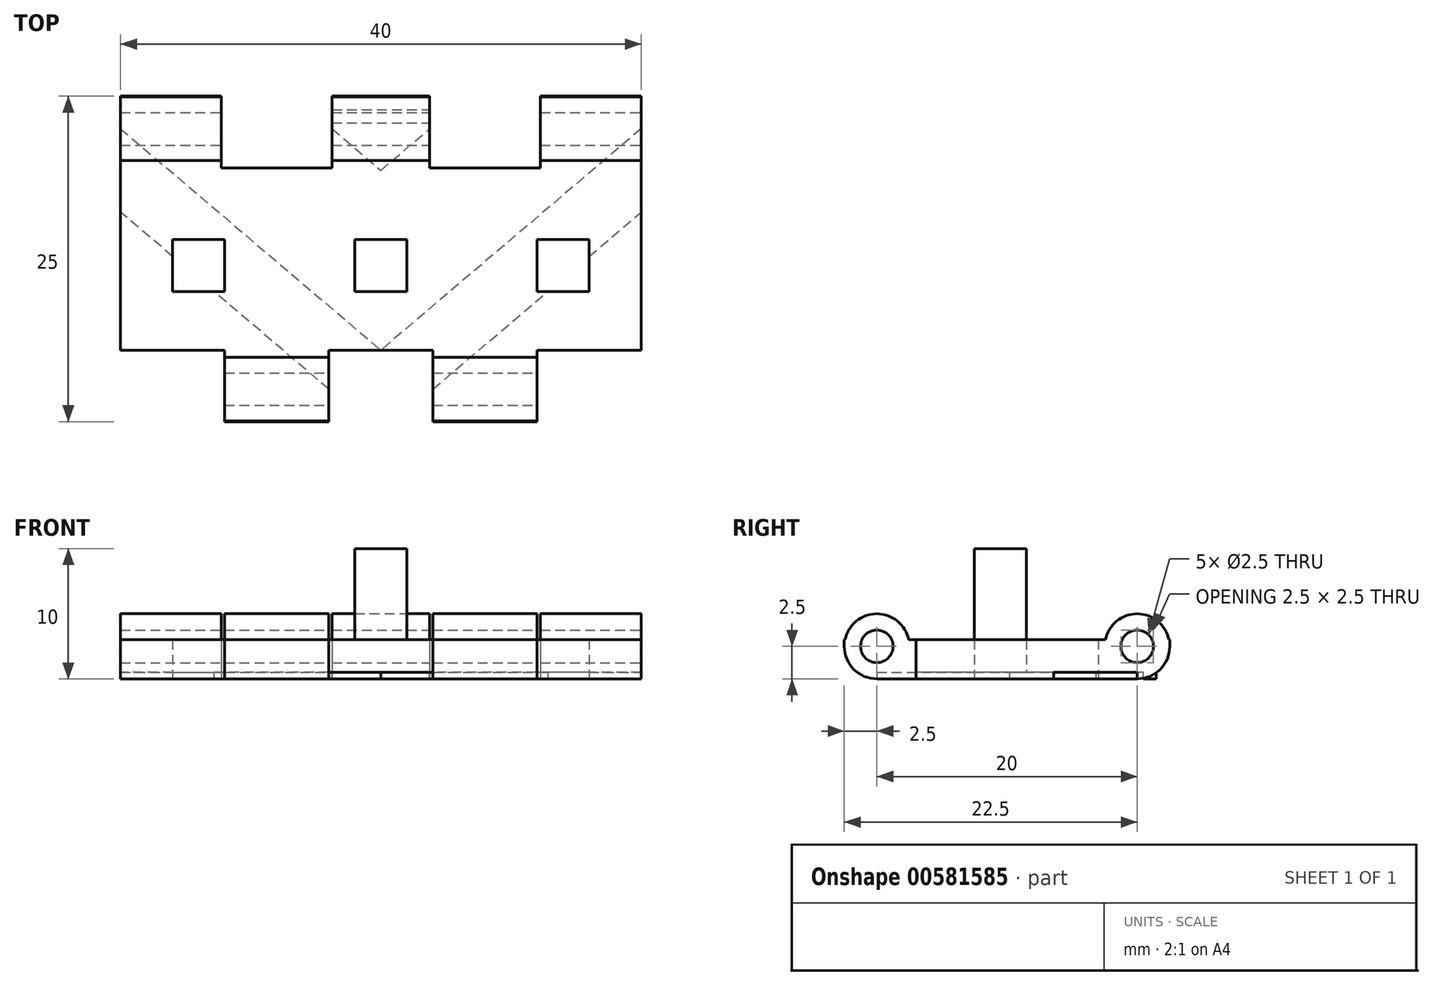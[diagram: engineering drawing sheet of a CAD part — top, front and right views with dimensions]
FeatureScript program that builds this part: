
annotation { "Feature Type Name" : "Feature", "Feature Type Description" : "" }
export const myFeature = defineFeature(function(context is Context, id is Id, definition is map)
    precondition{}
    {
        {
            var Q0;
            Q0=qCreatedBy(makeId("Top.planeOp"),FACE);
            var sketch = newSketch(context, id + "F0", { "sketchPlane" : qUnion([Q0])});
            skPoint(sketch, "E0.middle", {"position": v(0, 0) * mm});
            skLineSegment(sketch, "E1.top", {"start": v(-20, 15) * mm, "end": v(-12.25, 15) * mm});
            skLineSegment(sketch, "E1.left", {"start": v(-20, 10) * mm, "end": v(-20, 15) * mm});
            skLineSegment(sketch, "E1.right", {"start": v(-12.25, 10) * mm, "end": v(-12.25, 15) * mm});
            skLineSegment(sketch, "E2.top", {"start": v(20, 15) * mm, "end": v(12.25, 15) * mm});
            skLineSegment(sketch, "E2.left", {"start": v(20, 10) * mm, "end": v(20, 15) * mm});
            skLineSegment(sketch, "E2.right", {"start": v(12.25, 11) * mm, "end": v(12.25, 15) * mm});
            skLineSegment(sketch, "E3.top", {"start": v(-3.75, 15) * mm, "end": v(3.75, 15) * mm});
            skLineSegment(sketch, "E3.left", {"start": v(-3.75, 10) * mm, "end": v(-3.75, 15) * mm});
            skLineSegment(sketch, "E3.right", {"start": v(3.75, 11) * mm, "end": v(3.75, 15) * mm});
            skLineSegment(sketch, "E4.top", {"start": v(-20, -6) * mm, "end": v(-12, -6) * mm});
            skLineSegment(sketch, "E4.right", {"start": v(-12, -10) * mm, "end": v(-12, -6) * mm});
            skLineSegment(sketch, "E5.top", {"start": v(20, -6) * mm, "end": v(12, -6) * mm});
            skLineSegment(sketch, "E5.right", {"start": v(12, -10) * mm, "end": v(12, -6) * mm});
            skLineSegment(sketch, "E6.top", {"start": v(4, -6) * mm, "end": v(-4, -6) * mm});
            skLineSegment(sketch, "E6.left", {"start": v(4, -10) * mm, "end": v(4, -6) * mm});
            skLineSegment(sketch, "E6.right", {"start": v(-4, -10) * mm, "end": v(-4, -6) * mm});
            skLineSegment(sketch, "E7", {"start": v(-20, 10) * mm, "end": v(-20, -6) * mm});
            skLineSegment(sketch, "E8", {"start": v(-12, -10) * mm, "end": v(-4, -10) * mm});
            skLineSegment(sketch, "E9", {"start": v(4, -10) * mm, "end": v(12, -10) * mm});
            skLineSegment(sketch, "E10", {"start": v(20, -6) * mm, "end": v(20, 10) * mm});
            skLineSegment(sketch, "E11", {"start": v(-12.25, 10) * mm, "end": v(-3.75, 10) * mm});
            skLineSegment(sketch, "E12", {"start": v(3.75, 11) * mm, "end": v(12.25, 11) * mm});
            skSolve(sketch);
        }
        {
            var Q0;
            Q0=makeQuery(id+"F0.imprint","IMPRINT",FACE,{"disambiguationData":[TD([[makeQuery(id+"F0.imprint","IMPRINT",EDGE,{"derivedFrom":sQuery(id+"F0.wireOp",EDGE,"E1.top")}),-1.0]])]});
            var sketch = newSketch(context, id + "F1", { "sketchPlane" : qUnion([Q0])});
            skLineSegment(sketch, "E13.bottom", {"start": v(-16, 0) * mm, "end": v(-12, 0) * mm});
            skLineSegment(sketch, "E13.top", {"start": v(-16, 4) * mm, "end": v(-12, 4) * mm});
            skLineSegment(sketch, "E13.left", {"start": v(-16, 0) * mm, "end": v(-16, 4) * mm});
            skLineSegment(sketch, "E13.right", {"start": v(-12, 0) * mm, "end": v(-12, 4) * mm});
            skLineSegment(sketch, "E14.bottom", {"start": v(16, 0) * mm, "end": v(12, 0) * mm});
            skLineSegment(sketch, "E14.top", {"start": v(16, 4) * mm, "end": v(12, 4) * mm});
            skLineSegment(sketch, "E14.left", {"start": v(16, 0) * mm, "end": v(16, 4) * mm});
            skLineSegment(sketch, "E14.right", {"start": v(12, 0) * mm, "end": v(12, 4) * mm});
            skSolve(sketch);
        }
        {
            var Q0;
            Q0=makeQuery(id+"F0.imprint","IMPRINT",FACE,{"disambiguationData":[TD([[makeQuery(id+"F0.imprint","IMPRINT",EDGE,{"derivedFrom":sQuery(id+"F0.wireOp",EDGE,"E1.top")}),-1.0]])]});
            extrude(context, id + "F2", {"entities" : qUnion([Q0]), "depth" : 3 * mm, "offsetDistance" : 25 * mm});
        }
        {
            var Q0;
            Q0 = qSketchRegion(id + "F1", true);
            extrude(context, id + "F3", {"entities" : qUnion([Q0]), "operationType" : NewBodyOperationType.REMOVE, "depth" : 3 * mm, "offsetDistance" : 25 * mm});
        }
        {
            var Q0;
            Q0=qCreatedBy(makeId("Top.planeOp"),FACE);
            var sketch = newSketch(context, id + "F4", { "sketchPlane" : qUnion([Q0])});
            skLineSegment(sketch, "E15.bottom", {"start": v(2, 0) * mm, "end": v(-2, 0) * mm});
            skLineSegment(sketch, "E15.top", {"start": v(2, 4) * mm, "end": v(-2, 4) * mm});
            skLineSegment(sketch, "E15.left", {"start": v(2, 0) * mm, "end": v(2, 4) * mm});
            skLineSegment(sketch, "E15.right", {"start": v(-2, 0) * mm, "end": v(-2, 4) * mm});
            skSolve(sketch);
        }
        {
            var Q0;
            Q0 = qSketchRegion(id + "F4", true);
            extrude(context, id + "F5", {"entities" : qUnion([Q0]), "operationType" : NewBodyOperationType.ADD, "depth" : 10 * mm, "offsetDistance" : 25 * mm});
        }
        {
            var Q0;
            Q0=makeQuery(id+"F2.opExtrude","SWEPT_FACE",FACE,{"disambiguationData":[OSD([sQuery(id+"F0.wireOp",EDGE,"E2.left"),sQuery(id+"F0.wireOp",EDGE,"E10")])]});
            var sketch = newSketch(context, id + "F6", { "sketchPlane" : qUnion([Q0])});
            skCircle(sketch, "E16", {"center": v(12.5, 2.5) * mm, "radius": 2.5 * mm});
            skCircle(sketch, "E17", {"center": v(12.5, 2.5) * mm, "radius": 1.25 * mm});
            skSolve(sketch);
        }
        {
            var Q0;
            {var subQ0=sQuery(id+"F6.wireOp",EDGE,"E16");var subQ1=makeQuery(id+"F2.opExtrude","CAP_EDGE",EDGE,{"disambiguationData":[OSD([sQuery(id+"F0.wireOp",EDGE,"E2.left"),sQuery(id+"F0.wireOp",EDGE,"E10")])],"isStart":false});var subQ2=makeQuery(id+"F6.imprint","INTERSECT",VERTEX,{"disambiguationData":[OD(0.0)],"derivedFrom":[subQ1,subQ0]});Q0=makeQuery(id+"F6.imprint","IMPRINT",FACE,{"disambiguationData":[TD([[makeQuery(id+"F6.imprint","IMPRINT",EDGE,{"disambiguationData":[TD([[subQ2,-1.0]])],"derivedFrom":subQ0}),1.0]])]});}
            extrude(context, id + "F7", {"entities" : qUnion([Q0]), "operationType" : NewBodyOperationType.ADD, "oppositeDirection" : true, "depth" : 40 * mm, "offsetDistance" : 25 * mm});
        }
        {
            var Q0;
            {var subQ0=sQuery(id+"F6.wireOp",EDGE,"E17");var subQ1=makeQuery(id+"F2.opExtrude","CAP_EDGE",EDGE,{"disambiguationData":[OSD([sQuery(id+"F0.wireOp",EDGE,"E2.left"),sQuery(id+"F0.wireOp",EDGE,"E10")])],"isStart":false});var subQ2=makeQuery(id+"F6.imprint","INTERSECT",VERTEX,{"disambiguationData":[OD(0.0)],"derivedFrom":[subQ1,subQ0]});Q0=makeQuery(id+"F6.imprint","IMPRINT",FACE,{"disambiguationData":[TD([[makeQuery(id+"F6.imprint","IMPRINT",EDGE,{"disambiguationData":[TD([[subQ2,1.0]])],"derivedFrom":subQ0}),1.0]])]});}
            extrude(context, id + "F8", {"entities" : qUnion([Q0]), "operationType" : NewBodyOperationType.REMOVE, "oppositeDirection" : true, "depth" : 40 * mm, "offsetDistance" : 25 * mm});
        }
        {
            var Q0;
            {var subQ0=sQuery(id+"F6.wireOp",EDGE,"E16");var subQ1=sQuery(id+"F0.wireOp",EDGE,"E2.left");var subQ2=makeQuery(id+"F2.opExtrude","SWEPT_EDGE",EDGE,{"disambiguationData":[OSD([sQuery(id+"F0.wireOp",EDGE,"E2.top"),subQ1])]});var subQ3=makeQuery(id+"F6.imprint","INTERSECT",VERTEX,{"derivedFrom":[subQ2,subQ0]});Q0=makeQuery(id+"F6.imprint","IMPRINT",FACE,{"disambiguationData":[TD([[makeQuery(id+"F6.imprint","IMPRINT",EDGE,{"disambiguationData":[TD([[subQ3,1.0]])],"derivedFrom":subQ0}),-1.0]])]});}
            extrude(context, id + "F9", {"entities" : qUnion([Q0]), "operationType" : NewBodyOperationType.REMOVE, "oppositeDirection" : true, "depth" : 40 * mm, "offsetDistance" : 25 * mm});
        }
        {
            var Q0;
            Q0=makeQuery(id+"F2.opExtrude","CAP_FACE",FACE,{"disambiguationData":[OSD([sQuery(id+"F0.wireOp",EDGE,"E1.top"),sQuery(id+"F0.wireOp",EDGE,"E1.left"),sQuery(id+"F0.wireOp",EDGE,"E1.right"),sQuery(id+"F0.wireOp",EDGE,"E2.top"),sQuery(id+"F0.wireOp",EDGE,"E2.left"),sQuery(id+"F0.wireOp",EDGE,"E2.right"),sQuery(id+"F0.wireOp",EDGE,"E3.top"),sQuery(id+"F0.wireOp",EDGE,"E3.left"),sQuery(id+"F0.wireOp",EDGE,"E3.right"),sQuery(id+"F0.wireOp",EDGE,"E4.top"),sQuery(id+"F0.wireOp",EDGE,"E4.right"),sQuery(id+"F0.wireOp",EDGE,"E5.top"),sQuery(id+"F0.wireOp",EDGE,"E5.right"),sQuery(id+"F0.wireOp",EDGE,"E6.top"),sQuery(id+"F0.wireOp",EDGE,"E6.left"),sQuery(id+"F0.wireOp",EDGE,"E6.right"),sQuery(id+"F0.wireOp",EDGE,"E7"),sQuery(id+"F0.wireOp",EDGE,"E8"),sQuery(id+"F0.wireOp",EDGE,"E9"),sQuery(id+"F0.wireOp",EDGE,"E10"),sQuery(id+"F0.wireOp",EDGE,"E11"),sQuery(id+"F0.wireOp",EDGE,"E12")])],"isStart":true});
            var sketch = newSketch(context, id + "F10", { "sketchPlane" : qUnion([Q0])});
            skLineSegment(sketch, "E18.bottom", {"start": v(12.25, -11) * mm, "end": v(3.75, -11) * mm});
            skLineSegment(sketch, "E18.top", {"start": v(12.25, -16.51) * mm, "end": v(3.75, -16.51) * mm});
            skLineSegment(sketch, "E18.left", {"start": v(12.25, -11) * mm, "end": v(12.25, -16.51) * mm});
            skLineSegment(sketch, "E18.right", {"start": v(3.75, -11) * mm, "end": v(3.75, -16.51) * mm});
            skLineSegment(sketch, "E19.bottom", {"start": v(-3.75, -10) * mm, "end": v(-12.25, -10) * mm});
            skLineSegment(sketch, "E19.top", {"start": v(-3.75, -16.05) * mm, "end": v(-12.25, -16.05) * mm});
            skLineSegment(sketch, "E19.left", {"start": v(-3.75, -10) * mm, "end": v(-3.75, -16.05) * mm});
            skLineSegment(sketch, "E19.right", {"start": v(-12.25, -10) * mm, "end": v(-12.25, -16.05) * mm});
            skSolve(sketch);
        }
        {
            var Q0;
            Q0 = qSketchRegion(id + "F10", true);
            extrude(context, id + "F11", {"entities" : qUnion([Q0]), "operationType" : NewBodyOperationType.REMOVE, "oppositeDirection" : true, "depth" : 5 * mm, "offsetDistance" : 25 * mm});
        }
        {
            var Q0;
            Q0=makeQuery(id+"F2.opExtrude","SWEPT_FACE",FACE,{"disambiguationData":[OSD([sQuery(id+"F0.wireOp",EDGE,"E5.right")])]});
            var sketch = newSketch(context, id + "F12", { "sketchPlane" : qUnion([Q0])});
            skCircle(sketch, "E20", {"center": v(-7.5, 2.5) * mm, "radius": 2.5 * mm});
            skCircle(sketch, "E21", {"center": v(-7.5, 2.5) * mm, "radius": 1.25 * mm});
            skSolve(sketch);
        }
        {
            var Q0;
            {var subQ0=sQuery(id+"F0.wireOp",EDGE,"E5.right");var subQ1=makeQuery(id+"F2.opExtrude","CAP_EDGE",EDGE,{"disambiguationData":[OSD([subQ0])],"isStart":false});var subQ6=sQuery(id+"F12.wireOp",EDGE,"E21");var subQ7=makeQuery(id+"F12.imprint","INTERSECT",VERTEX,{"disambiguationData":[OD(0.0)],"derivedFrom":[subQ1,subQ6]});Q0=makeQuery(id+"F12.imprint","IMPRINT",FACE,{"disambiguationData":[TD([[makeQuery(id+"F12.imprint","IMPRINT",EDGE,{"disambiguationData":[TD([[subQ7,-1.0]])],"derivedFrom":subQ6}),-1.0]])]});}
            extrude(context, id + "F13", {"entities" : qUnion([Q0]), "operationType" : NewBodyOperationType.ADD, "oppositeDirection" : true, "depth" : 24 * mm, "offsetDistance" : 25 * mm});
        }
        {
            var Q0;
            Q0=makeQuery(id+"F2.opExtrude","CAP_FACE",FACE,{"disambiguationData":[OSD([sQuery(id+"F0.wireOp",EDGE,"E1.top"),sQuery(id+"F0.wireOp",EDGE,"E1.left"),sQuery(id+"F0.wireOp",EDGE,"E1.right"),sQuery(id+"F0.wireOp",EDGE,"E2.top"),sQuery(id+"F0.wireOp",EDGE,"E2.left"),sQuery(id+"F0.wireOp",EDGE,"E2.right"),sQuery(id+"F0.wireOp",EDGE,"E3.top"),sQuery(id+"F0.wireOp",EDGE,"E3.left"),sQuery(id+"F0.wireOp",EDGE,"E3.right"),sQuery(id+"F0.wireOp",EDGE,"E4.top"),sQuery(id+"F0.wireOp",EDGE,"E4.right"),sQuery(id+"F0.wireOp",EDGE,"E5.top"),sQuery(id+"F0.wireOp",EDGE,"E5.right"),sQuery(id+"F0.wireOp",EDGE,"E6.top"),sQuery(id+"F0.wireOp",EDGE,"E6.left"),sQuery(id+"F0.wireOp",EDGE,"E6.right"),sQuery(id+"F0.wireOp",EDGE,"E7"),sQuery(id+"F0.wireOp",EDGE,"E8"),sQuery(id+"F0.wireOp",EDGE,"E9"),sQuery(id+"F0.wireOp",EDGE,"E10"),sQuery(id+"F0.wireOp",EDGE,"E11"),sQuery(id+"F0.wireOp",EDGE,"E12")])],"isStart":true});
            var sketch = newSketch(context, id + "F14", { "sketchPlane" : qUnion([Q0])});
            skPoint(sketch, "E22.oppositeSnap0", {"position": v(4, 8) * mm});
            skLineSegment(sketch, "E22.bottom", {"start": v(-4, 6) * mm, "end": v(4, 6) * mm});
            skLineSegment(sketch, "E22.top", {"start": v(-4, 10.57) * mm, "end": v(4, 10.57) * mm});
            skLineSegment(sketch, "E22.left", {"start": v(-4, 6) * mm, "end": v(-4, 10.57) * mm});
            skLineSegment(sketch, "E22.right", {"start": v(4, 6) * mm, "end": v(4, 10.57) * mm});
            skSolve(sketch);
        }
        {
            var Q0;
            {var subQ3=sQuery(id+"F14.wireOp",EDGE,"E22.bottom");Q0=makeQuery(id+"F14.imprint","IMPRINT",FACE,{"disambiguationData":[TD([[makeQuery(id+"F14.imprint","IMPRINT",EDGE,{"derivedFrom":subQ3}),-1.0]])]});}
            extrude(context, id + "F15", {"entities" : qUnion([Q0]), "operationType" : NewBodyOperationType.REMOVE, "oppositeDirection" : true, "depth" : 5 * mm, "offsetDistance" : 25 * mm});
        }
        {
            var Q0;
            {var subQ0=sQuery(id+"F12.wireOp",EDGE,"E21");var subQ1=makeQuery(id+"F2.opExtrude","CAP_EDGE",EDGE,{"disambiguationData":[OSD([sQuery(id+"F0.wireOp",EDGE,"E5.right")])],"isStart":false});var subQ2=makeQuery(id+"F12.imprint","INTERSECT",VERTEX,{"disambiguationData":[OD(0.0)],"derivedFrom":[subQ1,subQ0]});Q0=makeQuery(id+"F12.imprint","IMPRINT",FACE,{"disambiguationData":[TD([[makeQuery(id+"F12.imprint","IMPRINT",EDGE,{"disambiguationData":[TD([[subQ2,1.0]])],"derivedFrom":subQ0}),1.0]])]});}
            extrude(context, id + "F16", {"entities" : qUnion([Q0]), "operationType" : NewBodyOperationType.REMOVE, "oppositeDirection" : true, "depth" : 24 * mm, "offsetDistance" : 25 * mm});
        }
        {
            var Q0;
            {var subQ0=sQuery(id+"F12.wireOp",EDGE,"E20");var subQ1=sQuery(id+"F0.wireOp",EDGE,"E5.right");var subQ4=makeQuery(id+"F2.opExtrude","CAP_EDGE",EDGE,{"disambiguationData":[OSD([subQ1])],"isStart":true});var subQ5=makeQuery(id+"F12.imprint","INTERSECT",VERTEX,{"derivedFrom":[subQ4,subQ0]});Q0=makeQuery(id+"F12.imprint","IMPRINT",FACE,{"disambiguationData":[TD([[makeQuery(id+"F12.imprint","IMPRINT",EDGE,{"disambiguationData":[TD([[subQ5,1.0]])],"derivedFrom":subQ0}),-1.0]])]});}
            extrude(context, id + "F17", {"entities" : qUnion([Q0]), "operationType" : NewBodyOperationType.REMOVE, "oppositeDirection" : true, "depth" : 24 * mm, "offsetDistance" : 25 * mm});
        }
        {
            var Q0;
            Q0=makeQuery(id+"F11.boolean.opBoolean","MERGE",FACE,{"derivedFrom":[makeQuery(id+"F2.opExtrude","SWEPT_FACE",FACE,{"disambiguationData":[OSD([sQuery(id+"F0.wireOp",EDGE,"E12")])]}),makeQuery(id+"F11.opExtrude","SWEPT_FACE",FACE,{"disambiguationData":[OSD([sQuery(id+"F10.wireOp",EDGE,"E18.bottom")])]})]});
            var Q1;
            Q1=makeQuery(id+"F11.boolean.opBoolean","MERGE",FACE,{"derivedFrom":[makeQuery(id+"F2.opExtrude","SWEPT_FACE",FACE,{"disambiguationData":[OSD([sQuery(id+"F0.wireOp",EDGE,"E11")])]}),makeQuery(id+"F11.opExtrude","SWEPT_FACE",FACE,{"disambiguationData":[OSD([sQuery(id+"F10.wireOp",EDGE,"E19.bottom")])]})]});
            extrude(context, id + "F18", {"entities" : qUnion([Q0, Q1]), "operationType" : NewBodyOperationType.REMOVE, "oppositeDirection" : true, "depth" : 1.5 * mm, "offsetDistance" : 25 * mm});
        }
        {
            var Q0;
            Q0=makeQuery(id+"F15.boolean.opBoolean","MERGE",FACE,{"derivedFrom":[makeQuery(id+"F2.opExtrude","SWEPT_FACE",FACE,{"disambiguationData":[OSD([sQuery(id+"F0.wireOp",EDGE,"E6.top")])]}),makeQuery(id+"F15.opExtrude","SWEPT_FACE",FACE,{"disambiguationData":[OSD([sQuery(id+"F14.wireOp",EDGE,"E22.bottom")])]})]});
            var Q1;
            Q1=makeQuery(id+"F2.opExtrude","SWEPT_FACE",FACE,{"disambiguationData":[OSD([sQuery(id+"F0.wireOp",EDGE,"E4.top")])]});
            var Q2;
            Q2=makeQuery(id+"F2.opExtrude","SWEPT_FACE",FACE,{"disambiguationData":[OSD([sQuery(id+"F0.wireOp",EDGE,"E5.top")])]});
            extrude(context, id + "F19", {"entities" : qUnion([Q0, Q1, Q2]), "operationType" : NewBodyOperationType.REMOVE, "oppositeDirection" : true, "depth" : 1.5 * mm, "offsetDistance" : 25 * mm});
        }
        {
            var Q0;
            Q0=makeQuery(id+"F2.opExtrude","CAP_FACE",FACE,{"disambiguationData":[OSD([sQuery(id+"F0.wireOp",EDGE,"E1.top"),sQuery(id+"F0.wireOp",EDGE,"E1.left"),sQuery(id+"F0.wireOp",EDGE,"E1.right"),sQuery(id+"F0.wireOp",EDGE,"E2.top"),sQuery(id+"F0.wireOp",EDGE,"E2.left"),sQuery(id+"F0.wireOp",EDGE,"E2.right"),sQuery(id+"F0.wireOp",EDGE,"E3.top"),sQuery(id+"F0.wireOp",EDGE,"E3.left"),sQuery(id+"F0.wireOp",EDGE,"E3.right"),sQuery(id+"F0.wireOp",EDGE,"E4.top"),sQuery(id+"F0.wireOp",EDGE,"E4.right"),sQuery(id+"F0.wireOp",EDGE,"E5.top"),sQuery(id+"F0.wireOp",EDGE,"E5.right"),sQuery(id+"F0.wireOp",EDGE,"E6.top"),sQuery(id+"F0.wireOp",EDGE,"E6.left"),sQuery(id+"F0.wireOp",EDGE,"E6.right"),sQuery(id+"F0.wireOp",EDGE,"E7"),sQuery(id+"F0.wireOp",EDGE,"E8"),sQuery(id+"F0.wireOp",EDGE,"E9"),sQuery(id+"F0.wireOp",EDGE,"E10"),sQuery(id+"F0.wireOp",EDGE,"E11"),sQuery(id+"F0.wireOp",EDGE,"E12")])],"isStart":true});
            var sketch = newSketch(context, id + "F20", { "sketchPlane" : qUnion([Q0])});
            skLineSegment(sketch, "E23", {"start": v(-20, -12.5) * mm, "end": v(0, 4.5) * mm});
            skLineSegment(sketch, "E24", {"start": v(0, 4.5) * mm, "end": v(-4, 7.5) * mm});
            skLineSegment(sketch, "E25", {"start": v(-4, 7.5) * mm, "end": v(-20, -6.1) * mm});
            skLineSegment(sketch, "E26", {"start": v(-20, -6.1) * mm, "end": v(-20, -12.5) * mm});
            skLineSegment(sketch, "E27", {"start": v(20, -12.5) * mm, "end": v(0, 4.5) * mm});
            skLineSegment(sketch, "E28", {"start": v(0, 4.5) * mm, "end": v(4, 7.5) * mm});
            skLineSegment(sketch, "E29", {"start": v(4, 7.5) * mm, "end": v(20, -6.1) * mm});
            skLineSegment(sketch, "E30", {"start": v(20, -6.1) * mm, "end": v(20, -12.5) * mm});
            skSolve(sketch);
        }
        {
            var Q0;
            {var subQ18=sQuery(id+"F20.wireOp",EDGE,"E23");Q0=makeQuery(id+"F20.imprint","IMPRINT",FACE,{"disambiguationData":[TD([[makeQuery(id+"F20.imprint","IMPRINT",EDGE,{"derivedFrom":subQ18}),1.0]])]});}
            var Q1;
            {var subQ11=sQuery(id+"F20.wireOp",EDGE,"E27");Q1=makeQuery(id+"F20.imprint","IMPRINT",FACE,{"disambiguationData":[TD([[makeQuery(id+"F20.imprint","IMPRINT",EDGE,{"derivedFrom":subQ11}),-1.0]])]});}
            extrude(context, id + "F21", {"entities" : qUnion([Q0, Q1]), "operationType" : NewBodyOperationType.REMOVE, "oppositeDirection" : true, "depth" : .5 * mm, "offsetDistance" : 25 * mm});
        }
        {
            var Q0;
            {var subQ0=sQuery(id+"F0.wireOp",EDGE,"E1.right");var subQ1=makeQuery(id+"F2.opExtrude","SWEPT_FACE",FACE,{"disambiguationData":[OSD([subQ0])]});var subQ2=sQuery(id+"F0.wireOp",EDGE,"E7");var subQ3=sQuery(id+"F0.wireOp",EDGE,"E1.left");var subQ5=sQuery(id+"F0.wireOp",EDGE,"E12");var subQ6=sQuery(id+"F0.wireOp",EDGE,"E11");var subQ7=sQuery(id+"F0.wireOp",EDGE,"E10");var subQ8=sQuery(id+"F0.wireOp",EDGE,"E3.right");var subQ9=sQuery(id+"F0.wireOp",EDGE,"E3.left");var subQ10=sQuery(id+"F0.wireOp",EDGE,"E3.top");var subQ11=sQuery(id+"F0.wireOp",EDGE,"E2.right");var subQ12=sQuery(id+"F0.wireOp",EDGE,"E2.left");var subQ13=sQuery(id+"F0.wireOp",EDGE,"E2.top");var subQ14=sQuery(id+"F0.wireOp",EDGE,"E1.top");var subQ15=makeQuery(id+"F2.opExtrude","CAP_FACE",FACE,{"disambiguationData":[OSD([subQ14,subQ3,subQ0,subQ13,subQ12,subQ11,subQ10,subQ9,subQ8,sQuery(id+"F0.wireOp",EDGE,"E4.top"),sQuery(id+"F0.wireOp",EDGE,"E4.right"),sQuery(id+"F0.wireOp",EDGE,"E5.top"),sQuery(id+"F0.wireOp",EDGE,"E5.right"),sQuery(id+"F0.wireOp",EDGE,"E6.top"),sQuery(id+"F0.wireOp",EDGE,"E6.left"),sQuery(id+"F0.wireOp",EDGE,"E6.right"),subQ2,sQuery(id+"F0.wireOp",EDGE,"E8"),sQuery(id+"F0.wireOp",EDGE,"E9"),subQ7,subQ6,subQ5])],"isStart":true});Q0=makeQuery(id+"F21.boolean.opBoolean","SPLIT",FACE,{"disambiguationData":[TD([subQ1])],"derivedFrom":subQ15});}
            var sketch = newSketch(context, id + "F22", { "sketchPlane" : qUnion([Q0])});
            skLineSegment(sketch, "E31", {"start": v(-3.75, -12.5) * mm, "end": v(0, -9.31) * mm});
            skLineSegment(sketch, "E32", {"start": v(0, -9.31) * mm, "end": v(3.75, -12.5) * mm});
            skLineSegment(sketch, "E33", {"start": v(3.75, -12.5) * mm, "end": v(3.75, -13.97) * mm});
            skLineSegment(sketch, "E34", {"start": v(3.75, -13.97) * mm, "end": v(-3.75, -13.97) * mm});
            skLineSegment(sketch, "E35", {"start": v(-3.75, -13.97) * mm, "end": v(-3.75, -12.5) * mm});
            skSolve(sketch);
        }
        {
            var Q0;
            Q0=makeQuery(id+"F22.imprint","IMPRINT",FACE,{"disambiguationData":[TD([[makeQuery(id+"F22.imprint","IMPRINT",EDGE,{"derivedFrom":sQuery(id+"F22.wireOp",EDGE,"E31")}),-1.0]])]});
            var Q1;
            Q1=makeQuery(id+"F22.imprint","IMPRINT",FACE,{"disambiguationData":[TD([[makeQuery(id+"F22.imprint","IMPRINT",EDGE,{"derivedFrom":sQuery(id+"F22.wireOp",EDGE,"E33")}),-1.0]])]});
            extrude(context, id + "F23", {"entities" : qUnion([Q0, Q1]), "operationType" : NewBodyOperationType.REMOVE, "oppositeDirection" : true, "depth" : .5 * mm, "offsetDistance" : 25 * mm});
        }
        {
            var Q0;
            Q0=makeQuery(id+"F2.opExtrude","SWEPT_FACE",FACE,{"disambiguationData":[OSD([sQuery(id+"F0.wireOp",EDGE,"E11")])]});
            extrude(context, id + "F24", {"entities" : qUnion([Q0]), "operationType" : NewBodyOperationType.REMOVE, "oppositeDirection" : true, "depth" : .5 * mm, "offsetDistance" : 25 * mm});
        }
        {
            var Q0;
            Q0=makeQuery(id+"F23.boolean.opBoolean","COPY",FACE,{"derivedFrom":makeQuery(id+"F23.opExtrude","CAP_FACE",FACE,{"disambiguationData":[OSD([sQuery(id+"F22.wireOp",EDGE,"E31"),sQuery(id+"F22.wireOp",EDGE,"E32"),sQuery(id+"F22.wireOp",EDGE,"E33"),sQuery(id+"F22.wireOp",EDGE,"E34"),sQuery(id+"F22.wireOp",EDGE,"E35")])],"isStart":false})});
            var sketch = newSketch(context, id + "F25", { "sketchPlane" : qUnion([Q0])});
            skLineSegment(sketch, "E36.bottom", {"start": v(-3.75, -13.97) * mm, "end": v(3.75, -13.97) * mm});
            skLineSegment(sketch, "E36.top", {"start": v(-3.75, -12.97) * mm, "end": v(3.75, -12.97) * mm});
            skLineSegment(sketch, "E36.left", {"start": v(-3.75, -13.97) * mm, "end": v(-3.75, -12.97) * mm});
            skLineSegment(sketch, "E36.right", {"start": v(3.75, -13.97) * mm, "end": v(3.75, -12.97) * mm});
            skSolve(sketch);
        }
        {
            var Q0;
            Q0=makeQuery(id+"F25.imprint","IMPRINT",FACE,{"disambiguationData":[TD([[makeQuery(id+"F25.imprint","IMPRINT",EDGE,{"derivedFrom":sQuery(id+"F25.wireOp",EDGE,"E36.bottom")}),-1.0]])]});
            extrude(context, id + "F26", {"entities" : qUnion([Q0]), "operationType" : NewBodyOperationType.ADD, "depth" : .5 * mm, "offsetDistance" : 25 * mm});
        }
    });
